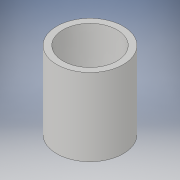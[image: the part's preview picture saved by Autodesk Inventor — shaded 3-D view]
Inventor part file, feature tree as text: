
AUTODESK INVENTOR PART (.ipt)
format: ipt  version: 2019.4 (Build 234330000, 330)  size: 95,232 bytes
history: native  units: mm
features: extrude x1, sketch x1
ambient origin geometry x8: Origin, YZ Plane, XZ Plane, XY Plane, X Axis, Y Axis, Z Axis, Center Point
bodies: Solid1 (feature_tree)
feature tree (2):
  extrude  "Extrusion1"  Depth=5.0mm
  sketch  "Sketch1"  dims[d0=3.5mm d1=4.3mm d2=5.0mm d3=0.0mm]
